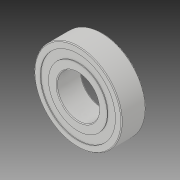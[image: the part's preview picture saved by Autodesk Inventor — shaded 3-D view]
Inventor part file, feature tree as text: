
AUTODESK INVENTOR PART (.ipt)
format: ipt  version: 2019 (Build 230136000, 136)  size: 144,896 bytes
history: native  units: in
note: dims shown in document units (in); Inventor stores cm internally (conversion verified against a paired STEP export)
features: fillet x1
ambient origin geometry x8: Origin, YZ Plane, XZ Plane, XY Plane, X Axis, Y Axis, Z Axis, Center Point
bodies: Solid1 (feature_tree)
feature tree (1):
  fillet  "Fillet1"  [1 undecoded]
note: 1 required parameter value undecoded (feature->parameter linkage not recoverable at this tier; creation-order binding heuristic only, values carry confidence <= 0.55)
